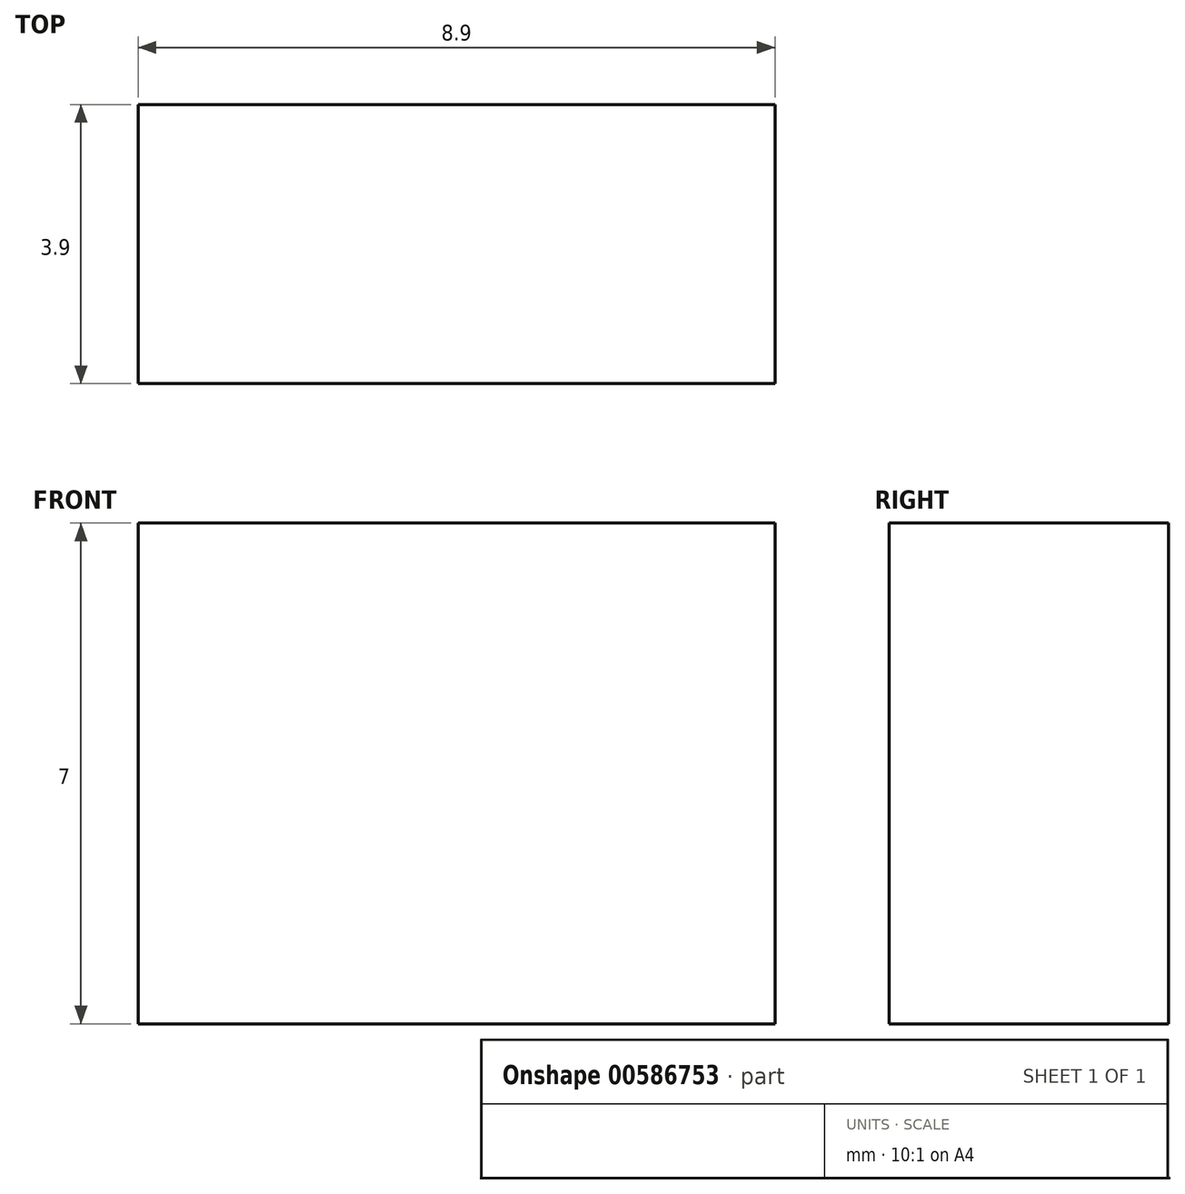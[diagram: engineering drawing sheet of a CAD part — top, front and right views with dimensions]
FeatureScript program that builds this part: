
annotation { "Feature Type Name" : "Feature", "Feature Type Description" : "" }
export const myFeature = defineFeature(function(context is Context, id is Id, definition is map)
    precondition{}
    {
        {
            var Q0;
            Q0=qCreatedBy(makeId("Top.planeOp"),FACE);
            var sketch = newSketch(context, id + "F0", { "sketchPlane" : qUnion([Q0])});
            skLineSegment(sketch, "E0.bottom", {"start": v(4.45, 1.95) * mm, "end": v(-4.45, 1.95) * mm});
            skLineSegment(sketch, "E0.top", {"start": v(4.45, -1.95) * mm, "end": v(-4.45, -1.95) * mm});
            skLineSegment(sketch, "E0.left", {"start": v(4.45, 1.95) * mm, "end": v(4.45, -1.95) * mm});
            skLineSegment(sketch, "E0.right", {"start": v(-4.45, 1.95) * mm, "end": v(-4.45, -1.95) * mm});
            skPoint(sketch, "E0.middle", {"position": v(0, 0) * mm});
            skSolve(sketch);
        }
        {
            var Q0;
            Q0=qSketchRegion(id+"F0",true);
            extrude(context, id + "F1", {"entities" : qUnion([Q0]), "depth" : 7 * mm, "offsetDistance" : 25 * mm});
        }
    });
